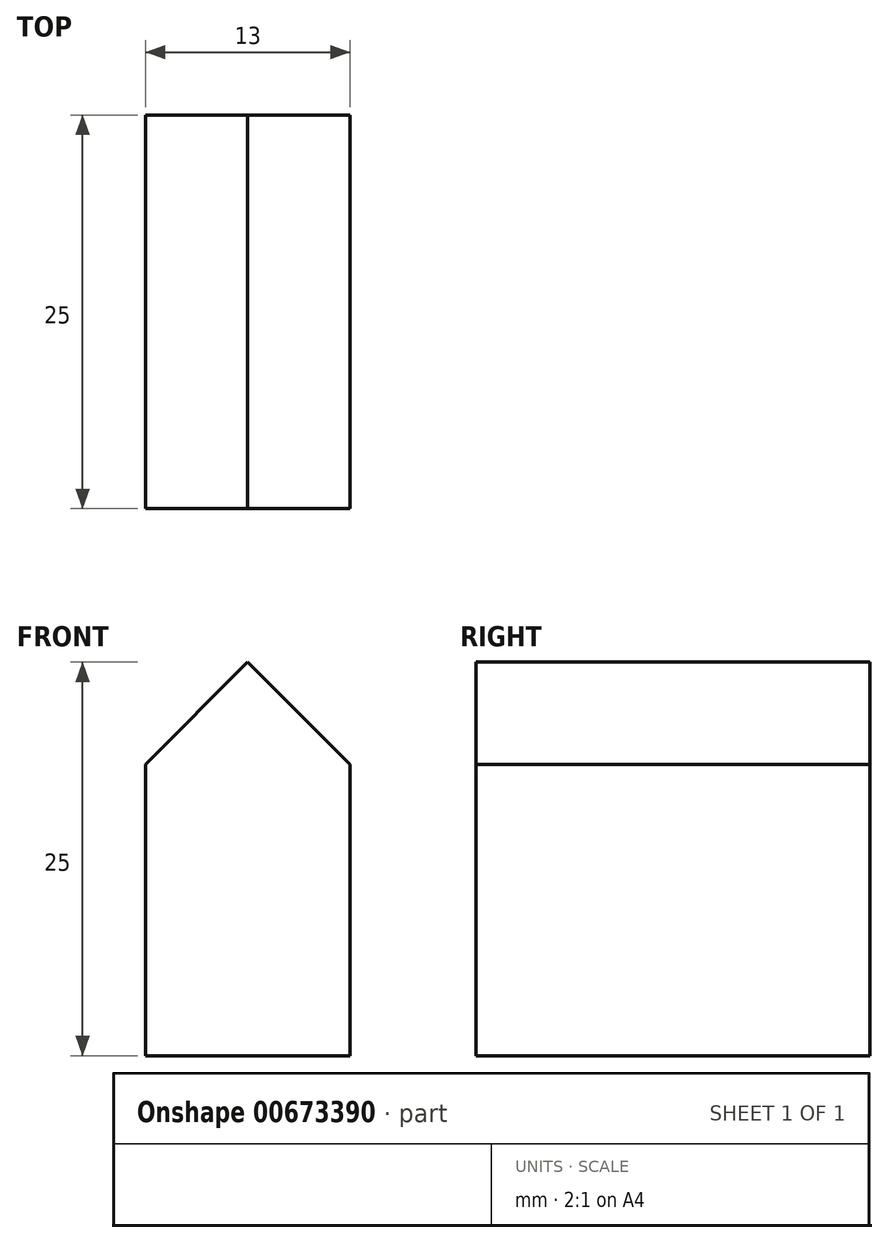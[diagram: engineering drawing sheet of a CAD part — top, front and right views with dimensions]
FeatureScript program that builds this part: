
annotation { "Feature Type Name" : "Feature", "Feature Type Description" : "" }
export const myFeature = defineFeature(function(context is Context, id is Id, definition is map)
    precondition{}
    {
        {
            var Q0;
            Q0=qCreatedBy(makeId("Front.planeOp"),FACE);
            var sketch = newSketch(context, id + "F0", { "sketchPlane" : qUnion([Q0])});
            skLineSegment(sketch, "E0.bottom", {"start": v(-6.5, 0) * mm, "end": v(6.5, 0) * mm});
            skLineSegment(sketch, "E0.top", {"start": v(-6.5, 18.5) * mm, "end": v(6.5, 18.5) * mm});
            skLineSegment(sketch, "E0.left", {"start": v(-6.5, 0) * mm, "end": v(-6.5, 18.5) * mm});
            skLineSegment(sketch, "E0.right", {"start": v(6.5, 0) * mm, "end": v(6.5, 18.5) * mm});
            skLineSegment(sketch, "E1", {"start": v(-6.5, 18.5) * mm, "end": v(0, 25) * mm});
            skLineSegment(sketch, "E2", {"start": v(0, 25) * mm, "end": v(6.5, 18.5) * mm});
            skSolve(sketch);
        }
        {
            var Q0;
            Q0 = qSketchRegion(id + "F0", true);
            extrude(context, id + "F1", {"entities" : qUnion([Q0]), "depth" : 25 * mm, "offsetDistance" : 25 * mm, "symmetric" : true});
        }
    });
